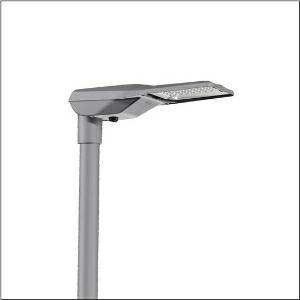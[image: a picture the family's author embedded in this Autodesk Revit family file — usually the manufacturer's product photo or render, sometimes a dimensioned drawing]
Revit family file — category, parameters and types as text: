
# Revit family: streetlight_sl_21_iq_mini___p0_8a_5xe2u31u08gb_cad6
name_source: partatom
category: Lighting Fixtures
units: mm (PartAtom-declared; Revit-internal decimal feet)

## family parameters
Cut with Voids When Loaded = No
Host = Face
Light Source = No
Part Type = Normal
Room Calculation Point = No
Round Connector Dimension = Use Diameter
Shared = No

## types (1)
- --- (1 x LED, 6040 lm, 39.8 W, 3000K)
    Apparent Load = 40 VA
    CIE Flux Codes = 33 69 96 100 100
    Color Rendering = 70
    Color Temperature = 3000K
    Default Elevation = 1800 mm
    Description = Streetlight SL 21 iQ mini, mast luminaire, primary light control with lens, of PMMA, primary optical cover: cover, of toughened safety glass, transparent, light distribution: P0.8a, light emission: direct distribution, primary light characteristic: asymmetric, installation type: post-top, side-entry, LED, High Power LED, rated luminous flux: 6.040lm, luminous efficacy: 152lm/W, light colour: 730, colour temperature: 3000K, control gear: iQ-Street Remote, D4i with power reduction, control: pre-setting: logarithmic dimming characteristic, Street-Remote, Auto-Match, Temp-Guard, Lumen-Switch, Night-Set, Smart-Wire, Light-Fading, Desk-Remote (wireless, voltage-free reading and setting of iQ features in the workshop via application-optimized NFC function/RFID function), optimised constant luminous flux control (CLO 2.0), mains connection: 220..240V, AC, 50/60Hz, start of lifetime: 40W, end of service life: 41W, reduction: 18W, luminaire housing, of diecast aluminium, powder-coated, Siteco® metallic grey (DB 702S), corrosivity category C5 mid according to DIN EN ISO 12944, please order mast flange separately, inclination adjustable: 0°, 5°, 10°, 15°, sealing non-destructively replaceable, multi-level sealing system, length: 628mm, width: 235mm, height: 110mm, mast flange for spigot size: 42mm (side-entry): 5XC10008XM4, 60/48mm (side-entry/post-top): 5XC10108XM2, 76/60mm (side-entry/post-top): 5XC10108XM1, mounting height: 4..8m, Smart Interface below, protection rating (complete): IP66, insulation class (complete): insulation class II (safety insulation), certification: CE, ENEC, ENEC+, VDE, impact resistance: IK10, permissible operating ambient temperature for outdoor applications: -40..+50°C, standard-compliant lighting for roads and squares, packaging unit: 1 piece

Light Distribution: P0.8a
    Height = 110 mm
    Lamp = 1 x LED
    Lamp Light Flux = 6040 lm
    Lamp Power = 39.8 W
    Lamp count = 1
    Length = 625 mm
    Luminous efficacy = 152 lm/W
    Manufacturer = Siteco
    ModVariant = No
    Model = 5XE2U31U08GB
    Number of Poles = 1
    OnlyDefault = Yes
    Power Factor = 1
    Product Name = Streetlight SL 21 iQ mini | P0.8a
    Product group = mast luminaire | pylon top
    ProductGroupID = 6100
    Protection Class = Protection class II
    Protection Degree = IP 66
    RLX_Detail_Level = 1
    RLX_Emergency_Light_Flux = 0 lm
    RLX_Emergency_Type = 0
    RLX_Emergency_Type_DB = No
    RlxData = <blob elided: 26473 chars, md5=1f468164>
    Socket = socket
    Standby Power = 0 W
    System Light Flux = 6040 lm
    System Power = 40 W
    Type Comments = factory setting: luminous flux: 100 % | dim-lin: 254 | 800 mA
    Type Image = l_1003516.jpg
    URL = http://relux.com
    VarID = @adj_074216
    Voltage = 0 V
    Weight = 0.00 kg
    Width = 234 mm

## geometry (parser evidence)
native form markers: Blend x4, Sweep x11
no freeform markers — native parametric forms only
